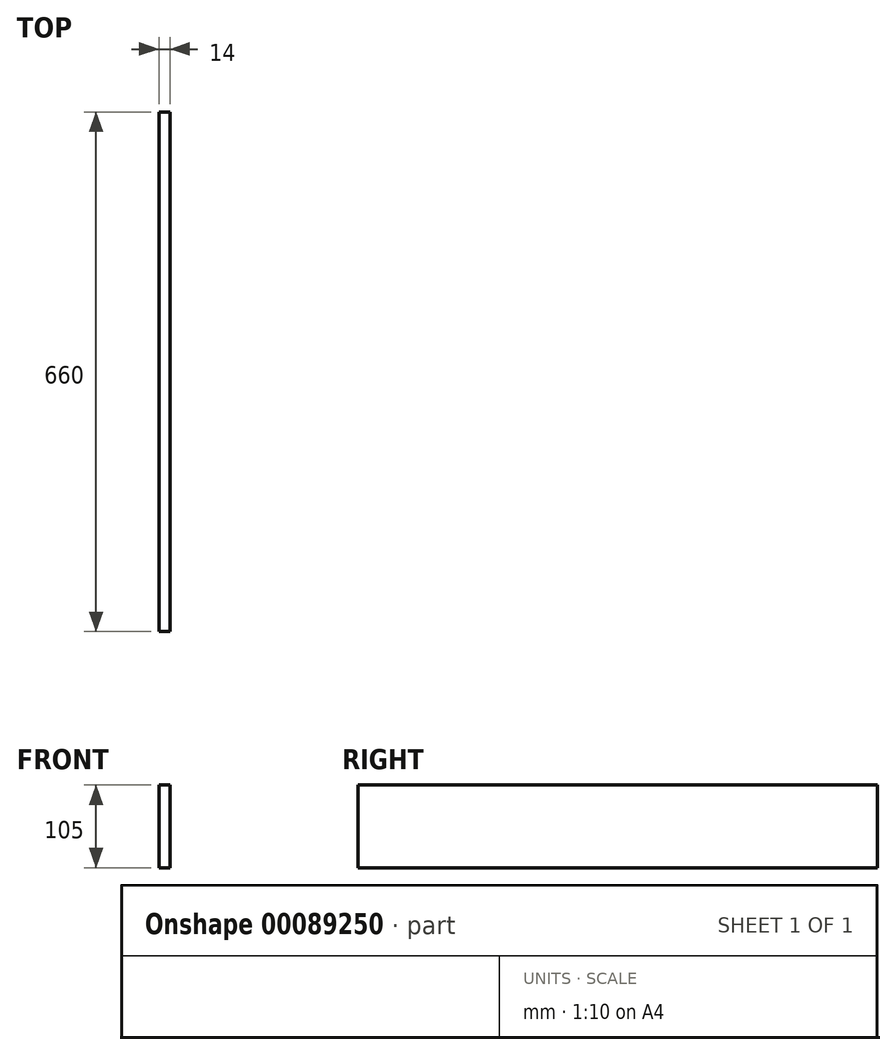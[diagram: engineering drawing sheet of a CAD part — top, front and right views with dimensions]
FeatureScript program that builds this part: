
annotation { "Feature Type Name" : "Feature", "Feature Type Description" : "" }
export const myFeature = defineFeature(function(context is Context, id is Id, definition is map)
    precondition{}
    {
        {
            var Q0;
            Q0=qCreatedBy(makeId("Right.planeOp"),FACE);
            var sketch = newSketch(context, id + "F0", { "sketchPlane" : qUnion([Q0])});
            skLineSegment(sketch, "E0.bottom", {"start": v(-330, 52.5) * mm, "end": v(330, 52.5) * mm});
            skLineSegment(sketch, "E0.top", {"start": v(-330, -52.5) * mm, "end": v(330, -52.5) * mm});
            skLineSegment(sketch, "E0.left", {"start": v(-330, 52.5) * mm, "end": v(-330, -52.5) * mm});
            skLineSegment(sketch, "E0.right", {"start": v(330, 52.5) * mm, "end": v(330, -52.5) * mm});
            skPoint(sketch, "E0.middle", {"position": v(0, 0) * mm});
            skSolve(sketch);
        }
        {
            var Q0;
            Q0=makeQuery(id+"F0.imprint","IMPRINT",FACE,{"disambiguationData":[TD([[makeQuery(id+"F0.imprint","IMPRINT",EDGE,{"derivedFrom":sQuery(id+"F0.wireOp",EDGE,"E0.bottom")}),-1.0]])]});
            extrude(context, id + "F1", {"entities" : qUnion([Q0]), "depth" : 14 * mm});
        }
    });
